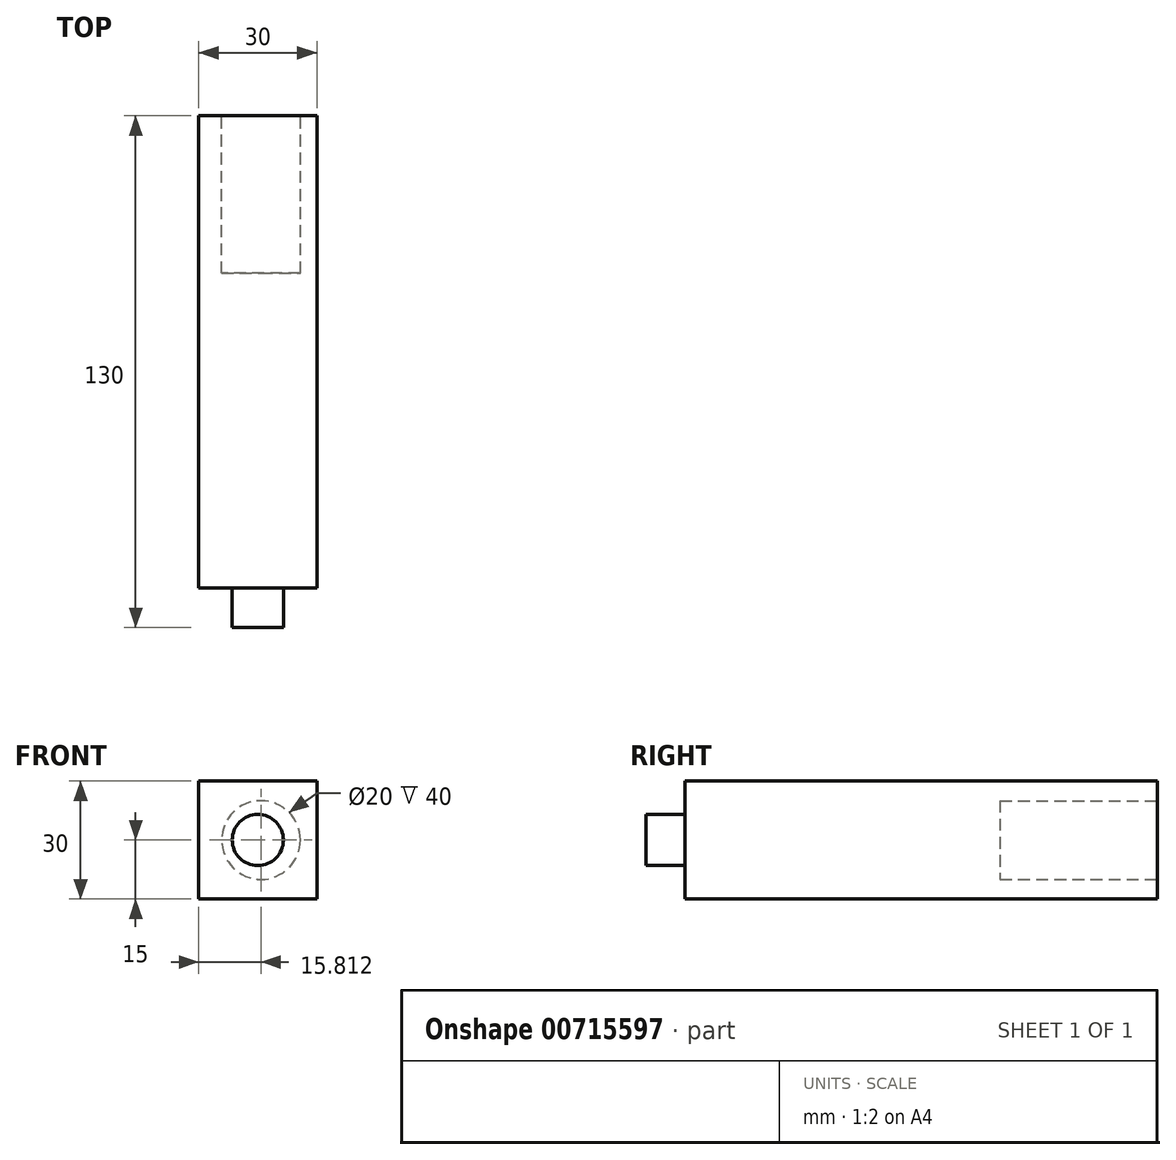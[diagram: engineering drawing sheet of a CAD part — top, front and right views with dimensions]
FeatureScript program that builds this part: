
annotation { "Feature Type Name" : "Feature", "Feature Type Description" : "" }
export const myFeature = defineFeature(function(context is Context, id is Id, definition is map)
    precondition{}
    {
        {
            var Q0;
            Q0=qCreatedBy(makeId("Front.planeOp"),FACE);
            var sketch = newSketch(context, id + "F0", { "sketchPlane" : qUnion([Q0])});
            skLineSegment(sketch, "E0.bottom", {"start": v(15, -15) * mm, "end": v(-15, -15) * mm});
            skLineSegment(sketch, "E0.top", {"start": v(15, 15) * mm, "end": v(-15, 15) * mm});
            skLineSegment(sketch, "E0.left", {"start": v(15, -15) * mm, "end": v(15, 15) * mm});
            skLineSegment(sketch, "E0.right", {"start": v(-15, -15) * mm, "end": v(-15, 15) * mm});
            skPoint(sketch, "E0.middle", {"position": v(0, 0) * mm});
            skSolve(sketch);
        }
        {
            var Q0;
            Q0 = qSketchRegion(id + "F0", true);
            extrude(context, id + "F1", {"entities" : qUnion([Q0]), "endBound" : BoundingType.SYMMETRIC, "depth" : 120 * mm, "offsetDistance" : 25 * mm});
        }
        {
            var Q0;
            Q0=makeQuery(id+"F1.opExtrude","CAP_FACE",FACE,{"disambiguationData":[OSD([sQuery(id+"F0.wireOp",EDGE,"E0.bottom"),sQuery(id+"F0.wireOp",EDGE,"E0.top"),sQuery(id+"F0.wireOp",EDGE,"E0.left"),sQuery(id+"F0.wireOp",EDGE,"E0.right")])],"isStart":false});
            var sketch = newSketch(context, id + "F2", { "sketchPlane" : qUnion([Q0])});
            skCircle(sketch, "E1", {"center": v(0, 0) * mm, "radius": 6.5 * mm});
            skSolve(sketch);
        }
        {
            var Q0;
            Q0 = qSketchRegion(id + "F2", true);
            extrude(context, id + "F3", {"entities" : qUnion([Q0]), "operationType" : NewBodyOperationType.ADD, "depth" : 10 * mm, "offsetDistance" : 25 * mm});
        }
        {
            var Q0;
            Q0=makeQuery(id+"F1.opExtrude","CAP_FACE",FACE,{"disambiguationData":[OSD([sQuery(id+"F0.wireOp",EDGE,"E0.bottom"),sQuery(id+"F0.wireOp",EDGE,"E0.top"),sQuery(id+"F0.wireOp",EDGE,"E0.left"),sQuery(id+"F0.wireOp",EDGE,"E0.right")])],"isStart":true});
            var sketch = newSketch(context, id + "F4", { "sketchPlane" : qUnion([Q0])});
            skCircle(sketch, "E2", {"center": v(-0.81, 0) * mm, "radius": 10 * mm});
            skSolve(sketch);
        }
        {
            var Q0;
            Q0 = qSketchRegion(id + "F4", true);
            extrude(context, id + "F5", {"entities" : qUnion([Q0]), "operationType" : NewBodyOperationType.REMOVE, "oppositeDirection" : true, "depth" : 40 * mm, "offsetDistance" : 25 * mm});
        }
    });
